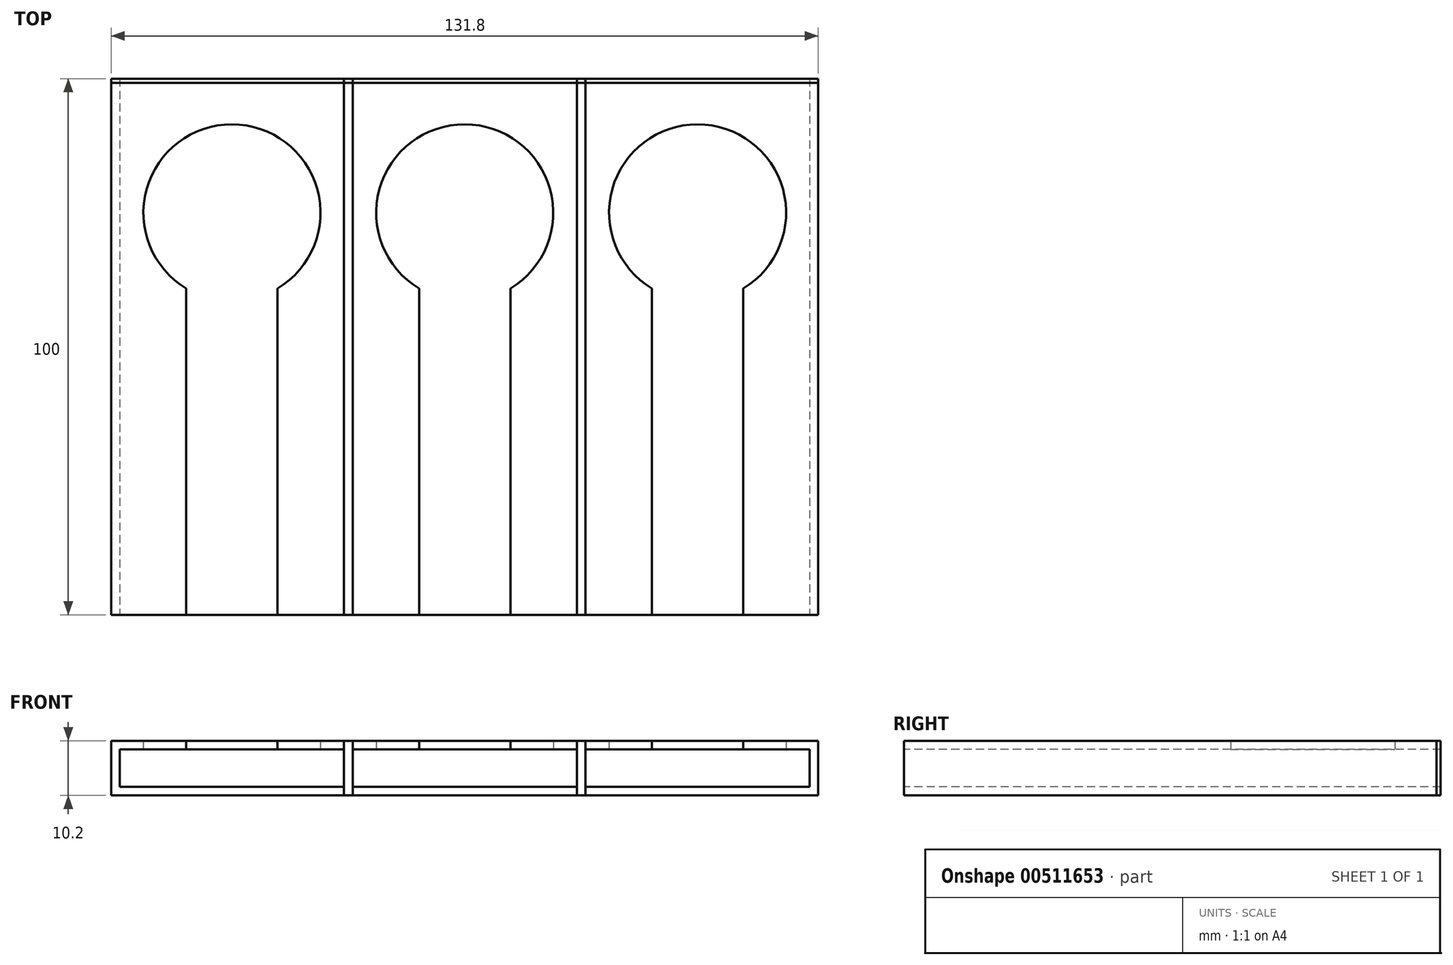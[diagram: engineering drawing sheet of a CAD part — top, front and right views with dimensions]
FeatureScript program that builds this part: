
annotation { "Feature Type Name" : "Feature", "Feature Type Description" : "" }
export const myFeature = defineFeature(function(context is Context, id is Id, definition is map)
    precondition{}
    {
        {
            var Q0;
            Q0=qCreatedBy(makeId("Top.planeOp"),FACE);
            var sketch = newSketch(context, id + "F0", { "sketchPlane" : qUnion([Q0])});
            skLineSegment(sketch, "E0.bottom", {"start": v(-56.34, 35.2) * mm, "end": v(-11.34, 35.2) * mm});
            skLineSegment(sketch, "E0.top", {"start": v(-56.34, -64.8) * mm, "end": v(-11.34, -64.8) * mm});
            skLineSegment(sketch, "E0.left", {"start": v(-56.34, 35.2) * mm, "end": v(-56.34, -64.8) * mm});
            skLineSegment(sketch, "E0.right", {"start": v(-11.34, 35.2) * mm, "end": v(-11.34, -64.8) * mm});
            skSolve(sketch);
        }
        {
            var Q0;
            Q0=makeQuery(id+"F0.imprint","IMPRINT",FACE,{"disambiguationData":[TD([[makeQuery(id+"F0.imprint","IMPRINT",EDGE,{"derivedFrom":sQuery(id+"F0.wireOp",EDGE,"E0.bottom")}),-1.0]])]});
            extrude(context, id + "F1", {"entities" : qUnion([Q0]), "depth" : 10.2 * mm});
        }
        {
            var Q0;
            Q0=makeQuery(id+"F1.opExtrude","CAP_FACE",FACE,{"disambiguationData":[OSD([sQuery(id+"F0.wireOp",EDGE,"E0.bottom"),sQuery(id+"F0.wireOp",EDGE,"E0.top"),sQuery(id+"F0.wireOp",EDGE,"E0.left"),sQuery(id+"F0.wireOp",EDGE,"E0.right")])],"isStart":false});
            var sketch = newSketch(context, id + "F2", { "sketchPlane" : qUnion([Q0])});
            skLineSegment(sketch, "E1.bottom", {"start": v(-42.34, -64.8) * mm, "end": v(-25.34, -64.8) * mm});
            skLineSegment(sketch, "E1.top", {"start": v(-42.34, 5.2) * mm, "end": v(-25.34, 5.2) * mm});
            skLineSegment(sketch, "E1.left", {"start": v(-42.34, -64.8) * mm, "end": v(-42.34, 5.2) * mm});
            skLineSegment(sketch, "E1.right", {"start": v(-25.34, -64.8) * mm, "end": v(-25.34, 5.2) * mm});
            skSolve(sketch);
        }
        {
            var Q0;
            Q0=qSketchRegion(id+"F2",true);
            extrude(context, id + "F3", {"entities" : qUnion([Q0]), "operationType" : NewBodyOperationType.REMOVE, "oppositeDirection" : true, "depth" : 8.6 * mm});
        }
        {
            var Q0;
            Q0=qCreatedBy(makeId("Top.planeOp"),FACE);
            var sketch = newSketch(context, id + "F4", { "sketchPlane" : qUnion([Q0])});
            skLineSegment(sketch, "E2.bottom", {"start": v(-56.34, 35.2) * mm, "end": v(-14.54, 35.2) * mm});
            skLineSegment(sketch, "E2.top", {"start": v(-56.34, -64.8) * mm, "end": v(-14.54, -64.8) * mm});
            skLineSegment(sketch, "E2.left", {"start": v(-56.34, 35.2) * mm, "end": v(-56.34, -64.8) * mm});
            skLineSegment(sketch, "E2.right", {"start": v(-14.54, 35.2) * mm, "end": v(-14.54, -64.8) * mm});
            skSolve(sketch);
        }
        {
            var Q0;
            Q0=makeQuery(id+"F4.imprint","IMPRINT",FACE,{"disambiguationData":[TD([[makeQuery(id+"F4.imprint","IMPRINT",EDGE,{"derivedFrom":sQuery(id+"F4.wireOp",EDGE,"E2.bottom")}),-1.0]])]});
            extrude(context, id + "F5", {"entities" : qUnion([Q0]), "depth" : 7 * mm});
        }
        {
            var Q0;
            Q0=makeQuery(id+"F5.opExtrude","SWEPT_BODY",BODY,{"disambiguationData":[OSD([sQuery(id+"F4.wireOp",EDGE,"E2.bottom"),sQuery(id+"F4.wireOp",EDGE,"E2.top"),sQuery(id+"F4.wireOp",EDGE,"E2.left"),sQuery(id+"F4.wireOp",EDGE,"E2.right")])]});
            transform(context, id + "F6", {"entities" : qUnion([Q0]), "transformType" : TransformType.TRANSLATION_3D, "dx" : 1.6 * mm, "dy" : 0 * mm, "dz" : 1.6 * mm, "makeCopy" : false});
        }
        {
            var Q0;
            Q0=makeQuery(id+"F5.opExtrude","SWEPT_BODY",BODY,{"disambiguationData":[OSD([sQuery(id+"F4.wireOp",EDGE,"E2.bottom"),sQuery(id+"F4.wireOp",EDGE,"E2.top"),sQuery(id+"F4.wireOp",EDGE,"E2.left"),sQuery(id+"F4.wireOp",EDGE,"E2.right")])]});
            var Q1;
            Q1=makeQuery(id+"F1.opExtrude","SWEPT_BODY",BODY,{"disambiguationData":[OSD([sQuery(id+"F0.wireOp",EDGE,"E0.bottom"),sQuery(id+"F0.wireOp",EDGE,"E0.top"),sQuery(id+"F0.wireOp",EDGE,"E0.left"),sQuery(id+"F0.wireOp",EDGE,"E0.right")])]});
            booleanBodies(context, id + "F7", {"operationType" : BooleanOperationType.SUBTRACTION, "tools" : qUnion([Q0]), "targets" : qUnion([Q1])});
        }
        {
            var Q0;
            Q0=qCreatedBy(makeId("Top.planeOp"),FACE);
            var sketch = newSketch(context, id + "F8", { "sketchPlane" : qUnion([Q0])});
            skCircle(sketch, "E3", {"center": v(-33.84, -64.8) * mm, "radius": 16.5 * mm});
            skSolve(sketch);
        }
        {
            var Q0;
            Q0=makeQuery(id+"F8.imprint","IMPRINT",FACE,{"disambiguationData":[TD([[makeQuery(id+"F8.imprint","IMPRINT",EDGE,{"derivedFrom":sQuery(id+"F8.wireOp",EDGE,"E3")}),1.0]])]});
            extrude(context, id + "F9", {"entities" : qUnion([Q0]), "depth" : 10 * mm});
        }
        {
            var Q0;
            Q0=makeQuery(id+"F9.opExtrude","SWEPT_BODY",BODY,{"disambiguationData":[OSD([sQuery(id+"F8.wireOp",EDGE,"E3")])]});
            transform(context, id + "F10", {"entities" : qUnion([Q0]), "transformType" : TransformType.TRANSLATION_3D, "dx" : 0 * mm, "dy" : 75 * mm, "dz" : 4 * mm, "makeCopy" : false});
        }
        {
            var Q0;
            Q0=makeQuery(id+"F9.opExtrude","SWEPT_BODY",BODY,{"disambiguationData":[OSD([sQuery(id+"F8.wireOp",EDGE,"E3")])]});
            var Q1;
            Q1=makeQuery(id+"F1.opExtrude","SWEPT_BODY",BODY,{"disambiguationData":[OSD([sQuery(id+"F0.wireOp",EDGE,"E0.bottom"),sQuery(id+"F0.wireOp",EDGE,"E0.top"),sQuery(id+"F0.wireOp",EDGE,"E0.left"),sQuery(id+"F0.wireOp",EDGE,"E0.right")])]});
            booleanBodies(context, id + "F11", {"operationType" : BooleanOperationType.SUBTRACTION, "tools" : qUnion([Q0]), "targets" : qUnion([Q1])});
        }
        {
            var Q0;
            Q0=makeQuery(id+"F1.opExtrude","SWEPT_BODY",BODY,{"disambiguationData":[OSD([sQuery(id+"F0.wireOp",EDGE,"E0.bottom"),sQuery(id+"F0.wireOp",EDGE,"E0.top"),sQuery(id+"F0.wireOp",EDGE,"E0.left"),sQuery(id+"F0.wireOp",EDGE,"E0.right")])]});
            transform(context, id + "F12", {"entities" : qUnion([Q0]), "transformType" : TransformType.TRANSLATION_3D, "dx" : 43.4 * mm, "dy" : 0 * mm, "dz" : 0 * mm, "makeCopy" : true});
        }
        {
            var Q0;
            Q0=makeQuery(id+"F12.opPattern","COPY",BODY,{"derivedFrom":makeQuery(id+"F1.opExtrude","SWEPT_BODY",BODY,{"disambiguationData":[OSD([sQuery(id+"F0.wireOp",EDGE,"E0.bottom"),sQuery(id+"F0.wireOp",EDGE,"E0.top"),sQuery(id+"F0.wireOp",EDGE,"E0.left"),sQuery(id+"F0.wireOp",EDGE,"E0.right")])]}),"instanceName":"1"});
            transform(context, id + "F13", {"entities" : qUnion([Q0]), "transformType" : TransformType.TRANSLATION_3D, "dx" : 43.4 * mm, "dy" : 0 * mm, "dz" : 0 * mm, "makeCopy" : true});
        }
        {
            var Q0;
            Q0=makeQuery(id+"F12.opPattern","COPY",FACE,{"derivedFrom":makeQuery(id+"F1.opExtrude","SWEPT_FACE",FACE,{"disambiguationData":[OSD([sQuery(id+"F0.wireOp",EDGE,"E0.bottom")])]}),"instanceName":"1"});
            var sketch = newSketch(context, id + "F14", { "sketchPlane" : qUnion([Q0])});
            skLineSegment(sketch, "E4.bottom", {"start": v(-75.46, 10.2) * mm, "end": v(56.34, 10.2) * mm});
            skLineSegment(sketch, "E4.top", {"start": v(-75.46, 0) * mm, "end": v(56.34, 0) * mm});
            skLineSegment(sketch, "E4.left", {"start": v(-75.46, 10.2) * mm, "end": v(-75.46, 0) * mm});
            skLineSegment(sketch, "E4.right", {"start": v(56.34, 10.2) * mm, "end": v(56.34, 0) * mm});
            skSolve(sketch);
        }
        {
            var Q0;
            Q0 = qSketchRegion(id + "F14", true);
            extrude(context, id + "F15", {"entities" : qUnion([Q0]), "oppositeDirection" : true, "depth" : 0.8 * mm});
        }
    });
